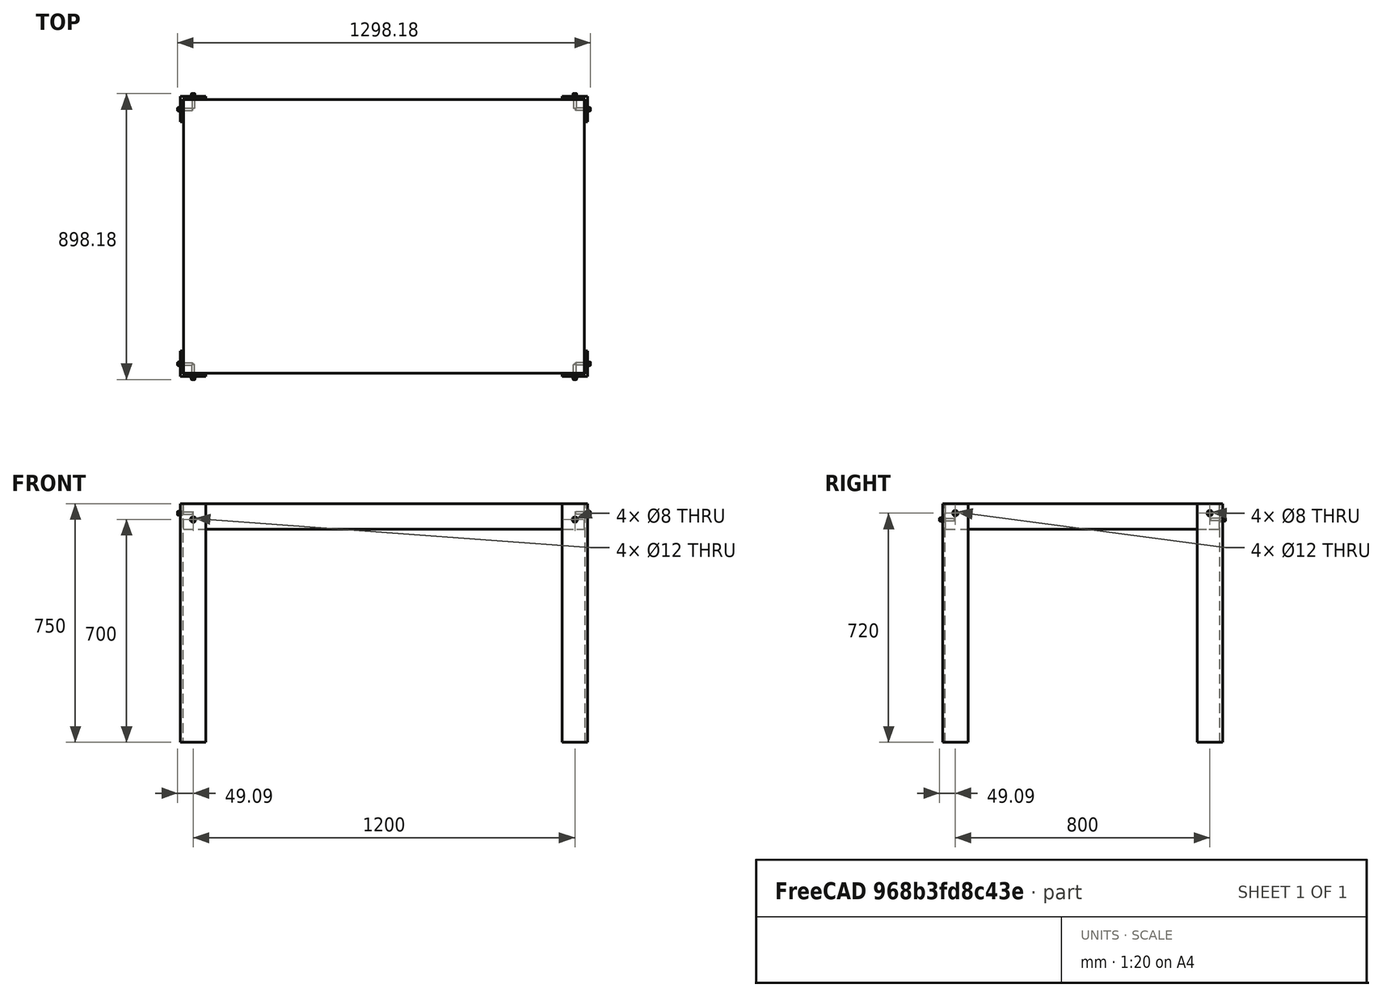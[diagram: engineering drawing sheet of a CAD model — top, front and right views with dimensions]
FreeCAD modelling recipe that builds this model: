
FCSTD DOCUMENT  (FreeCAD 0.18R4 (GitTag))
Label: table
License: CreativeCommons Attribution
LicenseURL: http://creativecommons.org/licenses/by/4.0/
objects: Part::Cut×12, Part::Box×9, Part::FeaturePython×8, Part::Cylinder×4, App::DocumentObjectGroup×1
note: 33 computed .brp shape members not serialized (recipe doc carries the construction recipe); baked Part::Feature solids carry a one-line shape summary decoded from their .brp

FEATURE [Part::Box] Box  label="Cube"
  AttacherType = Attacher::AttachEngine3D
  Height = 750
  Length = 80
  Width = 80
FEATURE [Part::Box] Box001  label="Cube001"
  AttacherType = Attacher::AttachEngine3D
  Height = 750
  Length = 80
  Placement = pos=(8,8,0) rot=(0,0,1;0rad)
  Width = 80
FEATURE [Part::Cut] Cut
  Base = -> Box
  Tool = -> Box001
FEATURE [Part::Box] Box002  label="Cube002"
  AttacherType = Attacher::AttachEngine3D
  Height = 750
  Length = 80
  Placement = pos=(0,800,0) rot=(0,0,1;0rad)
  Width = 80
FEATURE [Part::Box] Box003  label="Cube003"
  AttacherType = Attacher::AttachEngine3D
  Height = 750
  Length = 80
  Placement = pos=(8,792,0) rot=(0,0,1;0rad)
  Width = 80
FEATURE [Part::Cut] Cut001
  Base = -> Box002
  Tool = -> Box003
FEATURE [Part::Box] Box004  label="Cube004"
  AttacherType = Attacher::AttachEngine3D
  Height = 750
  Length = 80
  Placement = pos=(1200,0,0) rot=(0,0,1;0rad)
  Width = 80
FEATURE [Part::Box] Box005  label="Cube005"
  AttacherType = Attacher::AttachEngine3D
  Height = 750
  Length = 80
  Placement = pos=(1192,8,0) rot=(0,0,1;0rad)
  Width = 80
FEATURE [Part::Cut] Cut002
  Base = -> Box004
  Tool = -> Box005
FEATURE [Part::Box] Box006  label="Cube006"
  AttacherType = Attacher::AttachEngine3D
  Height = 750
  Length = 80
  Placement = pos=(1200,800,0) rot=(0,0,1;0rad)
  Width = 80
FEATURE [Part::Box] Box007  label="Cube007"
  AttacherType = Attacher::AttachEngine3D
  Height = 750
  Length = 80
  Placement = pos=(1192,792,0) rot=(0,0,1;0rad)
  Width = 80
FEATURE [Part::Cut] Cut003
  Base = -> Box006
  Tool = -> Box007
FEATURE [Part::Box] Box008  label="Top Portion"
  AttacherType = Attacher::AttachEngine3D
  Height = 80
  Length = 1260
  Placement = pos=(10,10,670) rot=(0,0,1;0rad)
  Width = 860
  expr: Width = 880 - 20
  expr: Length = 1280 - 20
FEATURE [Part::Cylinder] Cylinder
  Angle = 360
  AttacherType = Attacher::AttachEngine3D
  Height = 1300
  Placement = pos=(-10,40,720) rot=(0,1,0;1.5708rad)
  Radius = 6
FEATURE [Part::Cylinder] Cylinder001
  Angle = 360
  AttacherType = Attacher::AttachEngine3D
  Height = 1300
  Placement = pos=(-10,840,720) rot=(0,1,0;1.5708rad)
  Radius = 6
FEATURE [Part::Cylinder] Cylinder002
  Angle = 360
  AttacherType = Attacher::AttachEngine3D
  Height = 900
  Placement = pos=(40,-10,700) rot=(-1,0,0;1.5708rad)
  Radius = 6
FEATURE [Part::Cylinder] Cylinder003
  Angle = 360
  AttacherType = Attacher::AttachEngine3D
  Height = 900
  Placement = pos=(1240,-10,700) rot=(-1,0,0;1.5708rad)
  Radius = 6
FEATURE [Part::Cut] Cut004
  Base = -> Cut
  Tool = -> Cylinder
FEATURE [Part::Cut] Cut005
  Base = -> Cut002
  Tool = -> Cylinder
FEATURE [Part::Cut] Cut006  label="Foot 01"
  Base = -> Cut004
  Tool = -> Cylinder002
FEATURE [Part::Cut] Cut007
  Base = -> Cut001
  Tool = -> Cylinder002
FEATURE [Part::Cut] Cut008  label="Foot 02"
  Base = -> Cut007
  Tool = -> Cylinder001
FEATURE [Part::Cut] Cut009
  Base = -> Cut003
  Tool = -> Cylinder001
FEATURE [Part::Cut] Cut010  label="Foot 03"
  Base = -> Cut009
  Tool = -> Cylinder003
FEATURE [Part::Cut] Cut011  label="Foot 04"
  Base = -> Cut005
  Tool = -> Cylinder003
FEATURE [Part::FeaturePython] Screw  label="M8x40-Screw"  # Fasteners workbench fastener (typed FeaturePython)
  Placement = pos=(-2,40,720) rot=(0,-1,0;1.5708rad)
  diameter = 3
  invert = false
  length = 5
  lengthCustom = 16
  matchOuter = false
  offset = 0
  thread = false
  type = 1
FEATURE [Part::FeaturePython] Screw001  label="M8x40-Screw001"  # Fasteners workbench fastener (typed FeaturePython)
  Placement = pos=(-2,840,720) rot=(0,-1,0;1.5708rad)
  diameter = 3
  invert = false
  length = 5
  matchOuter = false
  offset = 0
  thread = false
  type = 1
FEATURE [Part::FeaturePython] Screw002  label="M8x40-Screw002"  # Fasteners workbench fastener (typed FeaturePython)
  Placement = pos=(1282,40,720) rot=(0,1,0;1.5708rad)
  diameter = 3
  invert = false
  length = 5
  matchOuter = false
  offset = 0
  thread = false
  type = 1
FEATURE [Part::FeaturePython] Screw003  label="M8x40-Screw003"  # Fasteners workbench fastener (typed FeaturePython)
  Placement = pos=(1282,840,720) rot=(0,1,0;1.5708rad)
  diameter = 3
  invert = false
  length = 5
  matchOuter = false
  offset = 0
  thread = false
  type = 1
FEATURE [Part::FeaturePython] Screw004  label="M8x40-Screw007"  # Fasteners workbench fastener (typed FeaturePython)
  Placement = pos=(40,882,700) rot=(-1,0,0;1.5708rad)
  diameter = 3
  invert = false
  length = 5
  matchOuter = false
  offset = 0
  thread = false
  type = 1
FEATURE [Part::FeaturePython] Screw005  label="M8x40-Screw005"  # Fasteners workbench fastener (typed FeaturePython)
  Placement = pos=(1240,-2,700) rot=(1,0,0;1.5708rad)
  diameter = 3
  invert = false
  length = 5
  matchOuter = false
  offset = 0
  thread = false
  type = 1
FEATURE [Part::FeaturePython] Screw006  label="M8x40-Screw006"  # Fasteners workbench fastener (typed FeaturePython)
  Placement = pos=(40,-2,700) rot=(1,0,0;1.5708rad)
  diameter = 3
  invert = false
  length = 5
  matchOuter = false
  offset = 0
  thread = false
  type = 1
FEATURE [Part::FeaturePython] Screw007  label="M8x40-Screw008"  # Fasteners workbench fastener (typed FeaturePython)
  Placement = pos=(1240,882,700) rot=(-1,0,0;1.5708rad)
  diameter = 3
  invert = false
  length = 5
  matchOuter = false
  offset = 0
  thread = false
  type = 1
FEATURE [App::DocumentObjectGroup] Group  label="Screws"
  Group = -> [Screw,Screw001,Screw002,Screw003,Screw004,Screw005,Screw006,Screw007]
